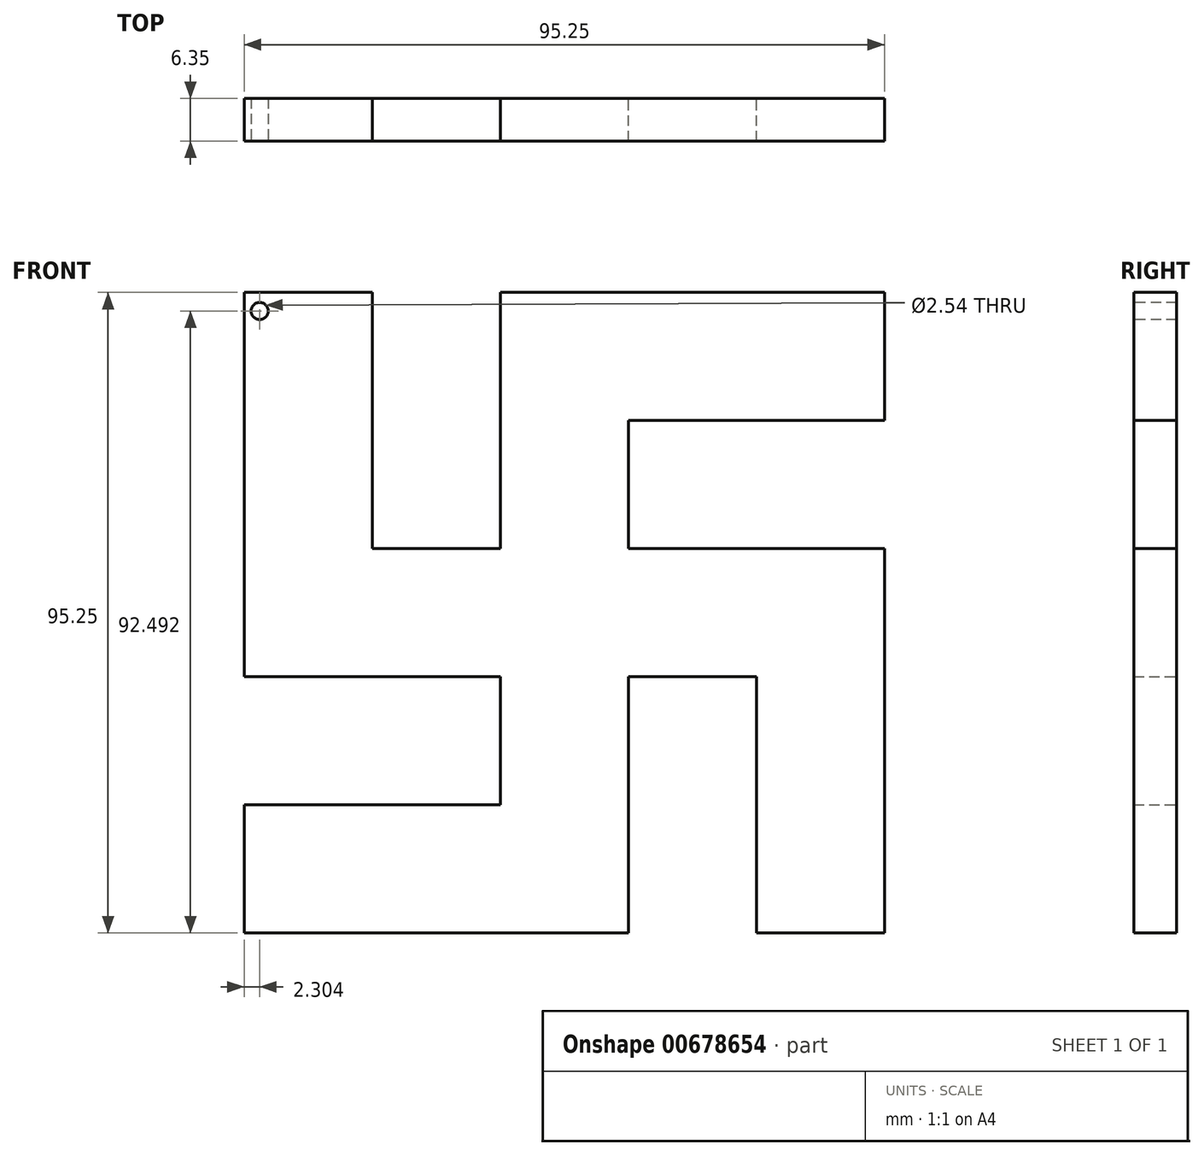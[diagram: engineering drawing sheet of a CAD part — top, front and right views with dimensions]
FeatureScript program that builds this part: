
annotation { "Feature Type Name" : "Feature", "Feature Type Description" : "" }
export const myFeature = defineFeature(function(context is Context, id is Id, definition is map)
    precondition{}
    {
        {
            var Q0;
            Q0=qCreatedBy(makeId("Front.planeOp"),FACE);
            var sketch = newSketch(context, id + "F0", { "sketchPlane" : qUnion([Q0])});
            skLineSegment(sketch, "E0", {"start": v(-48.98, 62.46) * mm, "end": v(-48.98, 5.3) * mm});
            skLineSegment(sketch, "E1", {"start": v(-48.98, 5.3) * mm, "end": v(27.22, 5.3) * mm});
            skLineSegment(sketch, "E2", {"start": v(27.22, 5.3) * mm, "end": v(27.22, -32.8) * mm});
            skLineSegment(sketch, "E3", {"start": v(27.22, -32.8) * mm, "end": v(46.27, -32.8) * mm});
            skLineSegment(sketch, "E4", {"start": v(46.27, -32.8) * mm, "end": v(46.27, 24.36) * mm});
            skLineSegment(sketch, "E5", {"start": v(46.27, 24.36) * mm, "end": v(-29.93, 24.36) * mm});
            skLineSegment(sketch, "E6", {"start": v(-29.93, 24.36) * mm, "end": v(-29.93, 62.46) * mm});
            skLineSegment(sketch, "E7", {"start": v(-29.93, 62.46) * mm, "end": v(-48.98, 62.46) * mm});
            skLineSegment(sketch, "E8", {"start": v(-48.98, -32.8) * mm, "end": v(-48.98, -13.74) * mm});
            skLineSegment(sketch, "E9", {"start": v(-48.98, -13.74) * mm, "end": v(-10.88, -13.74) * mm});
            skLineSegment(sketch, "E10", {"start": v(-10.88, -13.74) * mm, "end": v(-10.88, 62.46) * mm});
            skLineSegment(sketch, "E11", {"start": v(-10.88, 62.46) * mm, "end": v(46.27, 62.46) * mm});
            skLineSegment(sketch, "E12", {"start": v(46.27, 62.46) * mm, "end": v(46.27, 43.4) * mm});
            skLineSegment(sketch, "E13", {"start": v(46.27, 43.4) * mm, "end": v(8.17, 43.4) * mm});
            skLineSegment(sketch, "E14", {"start": v(8.17, 43.4) * mm, "end": v(8.17, -32.8) * mm});
            skLineSegment(sketch, "E15", {"start": v(8.17, -32.8) * mm, "end": v(-48.98, -32.8) * mm});
            skSolve(sketch);
        }
        {
            var Q0;
            {var subQ0=sQuery(id+"F0.wireOp",EDGE,"E11");Q0=makeQuery(id+"F0.imprint","IMPRINT",FACE,{"disambiguationData":[TD([[makeQuery(id+"F0.imprint","IMPRINT",EDGE,{"derivedFrom":subQ0}),-1.0]])]});}
            var Q1;
            {var subQ0=sQuery(id+"F0.wireOp",EDGE,"E10");var subQ1=sQuery(id+"F0.wireOp",EDGE,"E1");var subQ2=makeQuery(id+"F0.imprint","INTERSECT",VERTEX,{"derivedFrom":[subQ1,subQ0]});Q1=makeQuery(id+"F0.imprint","IMPRINT",FACE,{"disambiguationData":[TD([[makeQuery(id+"F0.imprint","IMPRINT",EDGE,{"disambiguationData":[TD([[subQ2,-1.0]])],"derivedFrom":subQ1}),1.0]])]});}
            var Q2;
            {var subQ1=sQuery(id+"F0.wireOp",EDGE,"E2");Q2=makeQuery(id+"F0.imprint","IMPRINT",FACE,{"disambiguationData":[TD([[makeQuery(id+"F0.imprint","IMPRINT",EDGE,{"derivedFrom":subQ1}),1.0]])]});}
            var Q3;
            Q3=makeQuery(id+"F0.imprint","IMPRINT",FACE,{"disambiguationData":[TD([[makeQuery(id+"F0.imprint","IMPRINT",EDGE,{"derivedFrom":sQuery(id+"F0.wireOp",EDGE,"E8")}),-1.0]])]});
            var Q4;
            {var subQ5=sQuery(id+"F0.wireOp",EDGE,"E0");Q4=makeQuery(id+"F0.imprint","IMPRINT",FACE,{"disambiguationData":[TD([[makeQuery(id+"F0.imprint","IMPRINT",EDGE,{"derivedFrom":subQ5}),1.0]])]});}
            extrude(context, id + "F1", {"entities" : qUnion([Q0, Q1, Q2, Q3, Q4]), "depth" : 6.35 * mm, "offsetDistance" : 25.4 * mm});
        }
        {
            var Q0;
            Q0=makeQuery(id+"F1.opExtrude","CAP_FACE",FACE,{"disambiguationData":[OSD([sQuery(id+"F0.wireOp",EDGE,"E0"),sQuery(id+"F0.wireOp",EDGE,"E1"),sQuery(id+"F0.wireOp",EDGE,"E2"),sQuery(id+"F0.wireOp",EDGE,"E3"),sQuery(id+"F0.wireOp",EDGE,"E4"),sQuery(id+"F0.wireOp",EDGE,"E5"),sQuery(id+"F0.wireOp",EDGE,"E6"),sQuery(id+"F0.wireOp",EDGE,"E7"),sQuery(id+"F0.wireOp",EDGE,"E8"),sQuery(id+"F0.wireOp",EDGE,"E9"),sQuery(id+"F0.wireOp",EDGE,"E10"),sQuery(id+"F0.wireOp",EDGE,"E11"),sQuery(id+"F0.wireOp",EDGE,"E12"),sQuery(id+"F0.wireOp",EDGE,"E13"),sQuery(id+"F0.wireOp",EDGE,"E14"),sQuery(id+"F0.wireOp",EDGE,"E15")])],"isStart":false});
            var sketch = newSketch(context, id + "F2", { "sketchPlane" : qUnion([Q0])});
            skCircle(sketch, "E16", {"center": v(-46.68, 59.7) * mm, "radius": 1.27 * mm});
            skSolve(sketch);
        }
        {
            var Q0;
            Q0=makeQuery(id+"F2.imprint","IMPRINT",FACE,{"disambiguationData":[TD([[makeQuery(id+"F2.imprint","IMPRINT",EDGE,{"derivedFrom":sQuery(id+"F2.wireOp",EDGE,"E16")}),1.0]])]});
            extrude(context, id + "F3", {"entities" : qUnion([Q0]), "operationType" : NewBodyOperationType.REMOVE, "oppositeDirection" : true, "depth" : 25.4 * mm, "offsetDistance" : 25.4 * mm});
        }
    });
